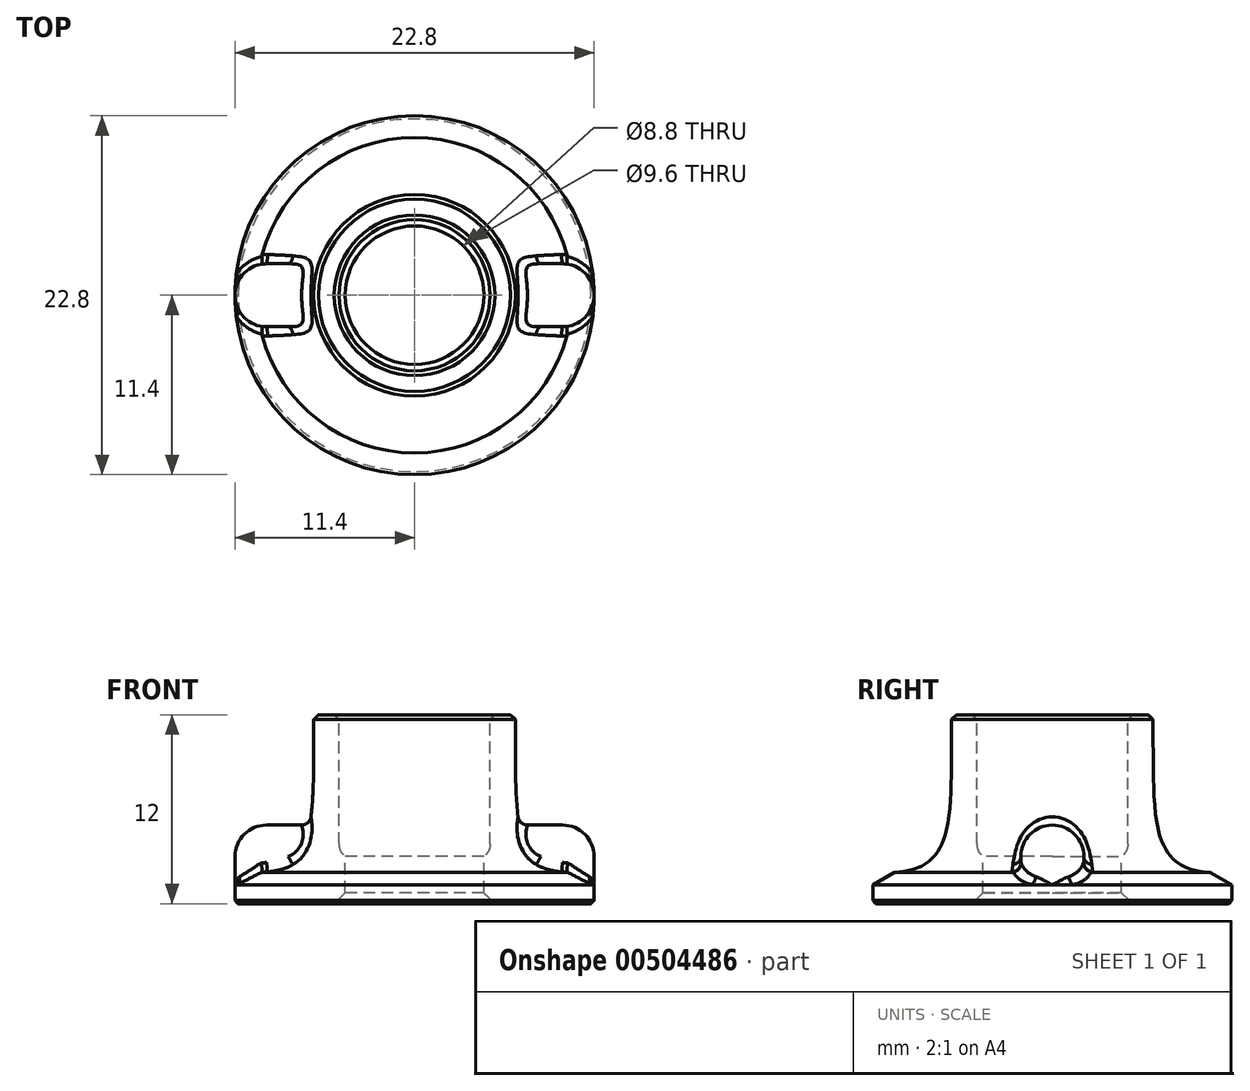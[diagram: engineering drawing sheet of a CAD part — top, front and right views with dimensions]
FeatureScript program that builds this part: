
annotation { "Feature Type Name" : "Feature", "Feature Type Description" : "" }
export const myFeature = defineFeature(function(context is Context, id is Id, definition is map)
    precondition{}
    {
        {
            var Q0;
            Q0=qCreatedBy(makeId("Front.planeOp"),FACE);
            var sketch = newSketch(context, id + "F0", { "sketchPlane" : qUnion([Q0])});
            skLineSegment(sketch, "E0", {"start": v(0, 0) * mm, "end": v(-11.4, 0) * mm});
            skLineSegment(sketch, "E1", {"start": v(-11.4, 0) * mm, "end": v(-11.4, 1.2) * mm});
            skLineSegment(sketch, "E2", {"start": v(-11.4, 1.2) * mm, "end": v(-10.01, 2) * mm});
            skLineSegment(sketch, "E3", {"start": v(-6.4, 10.22) * mm, "end": v(-6.4, 12) * mm});
            skLineSegment(sketch, "E4", {"start": v(-6.4, 12) * mm, "end": v(0, 12) * mm});
            skLineSegment(sketch, "E5", {"start": v(0, 12) * mm, "end": v(0, 0) * mm});
            skFitSpline(sketch, "E6", {"points": [v(-6.4, 12) * mm, v(-7.05, 3.76) * mm, v(-10.01, 2) * mm], "startDerivative": vector(0, -23.8) * mm, "endDerivative": vector(-13.91, -0.69) * mm});
            skLineSegment(sketch, "E7", {"start": v(-4.8, 12) * mm, "end": v(-4.8, 3) * mm});
            skLineSegment(sketch, "E8", {"start": v(-4.8, 3) * mm, "end": v(-4.4, 3) * mm});
            skLineSegment(sketch, "E9", {"start": v(-4.4, 3) * mm, "end": v(-4.4, 0) * mm});
            skSolve(sketch);
        }
        {
            var Q0;
            {var subQ6=sQuery(id+"F0.wireOp",EDGE,"E1");Q0=makeQuery(id+"F0.imprint","IMPRINT",FACE,{"disambiguationData":[TD([[makeQuery(id+"F0.imprint","IMPRINT",EDGE,{"derivedFrom":subQ6}),-1.0]])]});}
            var Q1;
            Q1=sQuery(id+"F0.wireOp",EDGE,"E5");
            revolve(context, id + "F1", {"entities" : qUnion([Q0]), "axis" : qUnion([Q1]), "revolveType" : RevolveType.FULL});
        }
        {
            var Q0;
            Q0=makeQuery(id+"F1.opRevolve","SWEPT_EDGE",EDGE,{"disambiguationData":[OSD([sQuery(id+"F0.wireOp",EDGE,"E4"),sQuery(id+"F0.wireOp",EDGE,"E7")])]});
            var Q1;
            Q1=makeQuery(id+"F1.opRevolve","SWEPT_EDGE",EDGE,{"disambiguationData":[OSD([sQuery(id+"F0.wireOp",EDGE,"E3"),sQuery(id+"F0.wireOp",EDGE,"E4"),sQuery(id+"F0.wireOp",EDGE,"E6")])]});
            chamfer(context, id + "F2", {"entities" : qUnion([Q0, Q1]), "width" : .3 * mm, "tangentPropagation" : true});
        }
        {
            var Q0;
            Q0=makeQuery(id+"F1.opRevolve","SWEPT_EDGE",EDGE,{"disambiguationData":[OSD([sQuery(id+"F0.wireOp",EDGE,"E7"),sQuery(id+"F0.wireOp",EDGE,"E8")])]});
            fillet(context, id + "F3", {"entities" : qUnion([Q0]), "radius" : 1 * mm, "allowEdgeOverflow" : false});
        }
        {
            var Q0;
            Q0=qCreatedBy(makeId("Top.planeOp"),FACE);
            cPlane(context, id + "F4", {"entities" : qUnion([Q0]), "cplaneType" : CPlaneType.OFFSET, "offset" : 5 * mm, "width" : 150 * mm, "height" : 150 * mm});
        }
        {
            var Q0;
            Q0=qCreatedBy(id+"F4.planeOp",FACE);
            var sketch = newSketch(context, id + "F5", { "sketchPlane" : qUnion([Q0])});
            skLineSegment(sketch, "E10.bottom", {"start": v(-9.4, -2) * mm, "end": v(9.4, -2) * mm});
            skLineSegment(sketch, "E10.top", {"start": v(-9.4, 2) * mm, "end": v(9.4, 2) * mm});
            skLineSegment(sketch, "E10.left", {"start": v(-11.4, 0) * mm, "end": v(-11.4, 0) * mm});
            skLineSegment(sketch, "E10.right", {"start": v(11.4, 0) * mm, "end": v(11.4, 0) * mm});
            skPoint(sketch, "E11.visualSharp", {"position": v(-11.4, 2) * mm});
            skArc(sketch, "E11.filletArc", {"start": v(-9.4, 2) * mm, "mid": v(-10.81, 1.41) * mm, "end": v(-11.4, 0) * mm});
            skPoint(sketch, "E12.visualSharp", {"position": v(-11.4, -2) * mm});
            skArc(sketch, "E12.filletArc", {"start": v(-11.4, 0) * mm, "mid": v(-10.81, -1.41) * mm, "end": v(-9.4, -2) * mm});
            skPoint(sketch, "E13.visualSharp", {"position": v(11.4, -2) * mm});
            skArc(sketch, "E13.filletArc", {"start": v(9.4, -2) * mm, "mid": v(10.81, -1.41) * mm, "end": v(11.4, 0) * mm});
            skPoint(sketch, "E14.visualSharp", {"position": v(11.4, 2) * mm});
            skArc(sketch, "E14.filletArc", {"start": v(11.4, 0) * mm, "mid": v(10.81, 1.41) * mm, "end": v(9.4, 2) * mm});
            skCircle(sketch, "E15", {"center": v(0, 0) * mm, "radius": 6.1 * mm});
            skSolve(sketch);
        }
        {
            var Q0;
            {var subQ1=sQuery(id+"F5.wireOp",EDGE,"E11.filletArc");Q0=makeQuery(id+"F5.imprint","IMPRINT",FACE,{"disambiguationData":[TD([[makeQuery(id+"F5.imprint","IMPRINT",EDGE,{"derivedFrom":subQ1}),1.0]])]});}
            var Q1;
            {var subQ1=sQuery(id+"F5.wireOp",EDGE,"E13.filletArc");Q1=makeQuery(id+"F5.imprint","IMPRINT",FACE,{"disambiguationData":[TD([[makeQuery(id+"F5.imprint","IMPRINT",EDGE,{"derivedFrom":subQ1}),1.0]])]});}
            var Q2;
            Q2=makeQuery(id+"F1.opRevolve","SWEPT_FACE",FACE,{"disambiguationData":[OSD([sQuery(id+"F0.wireOp",EDGE,"E2")])]});
            extrude(context, id + "F6", {"entities" : qUnion([Q0, Q1]), "operationType" : NewBodyOperationType.ADD, "oppositeDirection" : true, "endBoundEntityFace" : qUnion([Q2]), "depth" : 4 * mm});
        }
        {
            var Q0;
            {var subQ0=sQuery(id+"F5.wireOp",EDGE,"E10.bottom");Q0=makeQuery(id+"F6.opExtrude","CAP_EDGE",EDGE,{"disambiguationData":[OSD([subQ0]),TDD([makeQuery(id+"F5.imprint","IMPRINT",EDGE,{"disambiguationData":[TD([[makeQuery(id+"F5.imprint","INTERSECT",VERTEX,{"derivedFrom":[subQ0,sQuery(id+"F5.wireOp",EDGE,"E12.filletArc")]}),-1.0]])],"derivedFrom":subQ0})])],"isStart":true});}
            var Q1;
            {var subQ0=sQuery(id+"F5.wireOp",EDGE,"E10.bottom");Q1=makeQuery(id+"F6.opExtrude","CAP_EDGE",EDGE,{"disambiguationData":[OSD([subQ0]),TDD([makeQuery(id+"F5.imprint","IMPRINT",EDGE,{"disambiguationData":[TD([[makeQuery(id+"F5.imprint","INTERSECT",VERTEX,{"derivedFrom":[subQ0,sQuery(id+"F5.wireOp",EDGE,"E13.filletArc")]}),1.0]])],"derivedFrom":subQ0})])],"isStart":true});}
            fillet(context, id + "F7", {"entities" : qUnion([Q0, Q1]), "radius" : 2 * mm, "tangentPropagation" : true, "allowEdgeOverflow" : false});
        }
        {
            var Q0;
            Q0=makeQuery(id+"F1.opRevolve","SWEPT_EDGE",EDGE,{"disambiguationData":[OSD([sQuery(id+"F0.wireOp",EDGE,"E0"),sQuery(id+"F0.wireOp",EDGE,"E9")])]});
            chamfer(context, id + "F8", {"entities" : qUnion([Q0]), "width" : 0.7 * mm, "tangentPropagation" : true});
        }
        {
            var Q0;
            Q0=makeQuery(id+"F1.opRevolve","SWEPT_EDGE",EDGE,{"disambiguationData":[OSD([sQuery(id+"F0.wireOp",EDGE,"E0"),sQuery(id+"F0.wireOp",EDGE,"E1")])]});
            chamfer(context, id + "F9", {"entities" : qUnion([Q0]), "width" : .2 * mm, "tangentPropagation" : true});
        }
        {
            var Q0;
            {var subQ0=sQuery(id+"F5.wireOp",EDGE,"E10.top");Q0=makeQuery(id+"F7.opFillet","BLEND_EDGE",EDGE,{"blendedFrom":[makeQuery(id+"F6.opExtrude","CAP_EDGE",EDGE,{"disambiguationData":[OSD([subQ0]),TDD([makeQuery(id+"F5.imprint","IMPRINT",EDGE,{"disambiguationData":[TD([[makeQuery(id+"F5.imprint","INTERSECT",VERTEX,{"derivedFrom":[subQ0,sQuery(id+"F5.wireOp",EDGE,"E14.filletArc")]}),1.0]])],"derivedFrom":subQ0})])],"isStart":true}),makeQuery(id+"F1.opRevolve","SWEPT_FACE",FACE,{"disambiguationData":[OSD([sQuery(id+"F0.wireOp",EDGE,"E6")])]})],"blendedInto":[makeQuery(id+"F1.opRevolve","SWEPT_FACE",FACE,{"disambiguationData":[OSD([sQuery(id+"F0.wireOp",EDGE,"E6")])]})]});}
            var Q1;
            Q1=makeQuery(id+"F6.boolean.opBoolean","INTERSECT",EDGE,{"disambiguationData":[OD(1.0)],"derivedFrom":[makeQuery(id+"F1.opRevolve","SWEPT_FACE",FACE,{"disambiguationData":[OSD([sQuery(id+"F0.wireOp",EDGE,"E2")])]}),makeQuery(id+"F6.opExtrude","SWEPT_FACE",FACE,{"disambiguationData":[OSD([sQuery(id+"F5.wireOp",EDGE,"E13.filletArc"),sQuery(id+"F5.wireOp",EDGE,"E14.filletArc")])]})]});
            var Q2;
            {var subQ0=sQuery(id+"F5.wireOp",EDGE,"E10.top");Q2=makeQuery(id+"F6.boolean.opBoolean","INTERSECT",EDGE,{"derivedFrom":[makeQuery(id+"F1.opRevolve","SWEPT_FACE",FACE,{"disambiguationData":[OSD([sQuery(id+"F0.wireOp",EDGE,"E6")])]}),makeQuery(id+"F6.opExtrude","SWEPT_FACE",FACE,{"disambiguationData":[OSD([subQ0]),TDD([makeQuery(id+"F5.imprint","IMPRINT",EDGE,{"disambiguationData":[TD([[makeQuery(id+"F5.imprint","INTERSECT",VERTEX,{"derivedFrom":[subQ0,sQuery(id+"F5.wireOp",EDGE,"E11.filletArc")]}),-1.0]])],"derivedFrom":subQ0})])]})]});}
            var Q3;
            Q3=makeQuery(id+"F6.boolean.opBoolean","INTERSECT",EDGE,{"disambiguationData":[OD(1.0)],"derivedFrom":[makeQuery(id+"F1.opRevolve","SWEPT_FACE",FACE,{"disambiguationData":[OSD([sQuery(id+"F0.wireOp",EDGE,"E2")])]}),makeQuery(id+"F6.opExtrude","SWEPT_FACE",FACE,{"disambiguationData":[OSD([sQuery(id+"F5.wireOp",EDGE,"E11.filletArc"),sQuery(id+"F5.wireOp",EDGE,"E12.filletArc")])]})]});
            fillet(context, id + "F10", {"entities" : qUnion([Q0, Q1, Q2, Q3]), "radius" : 0.6 * mm, "tangentPropagation" : true, "allowEdgeOverflow" : false});
        }
    });
